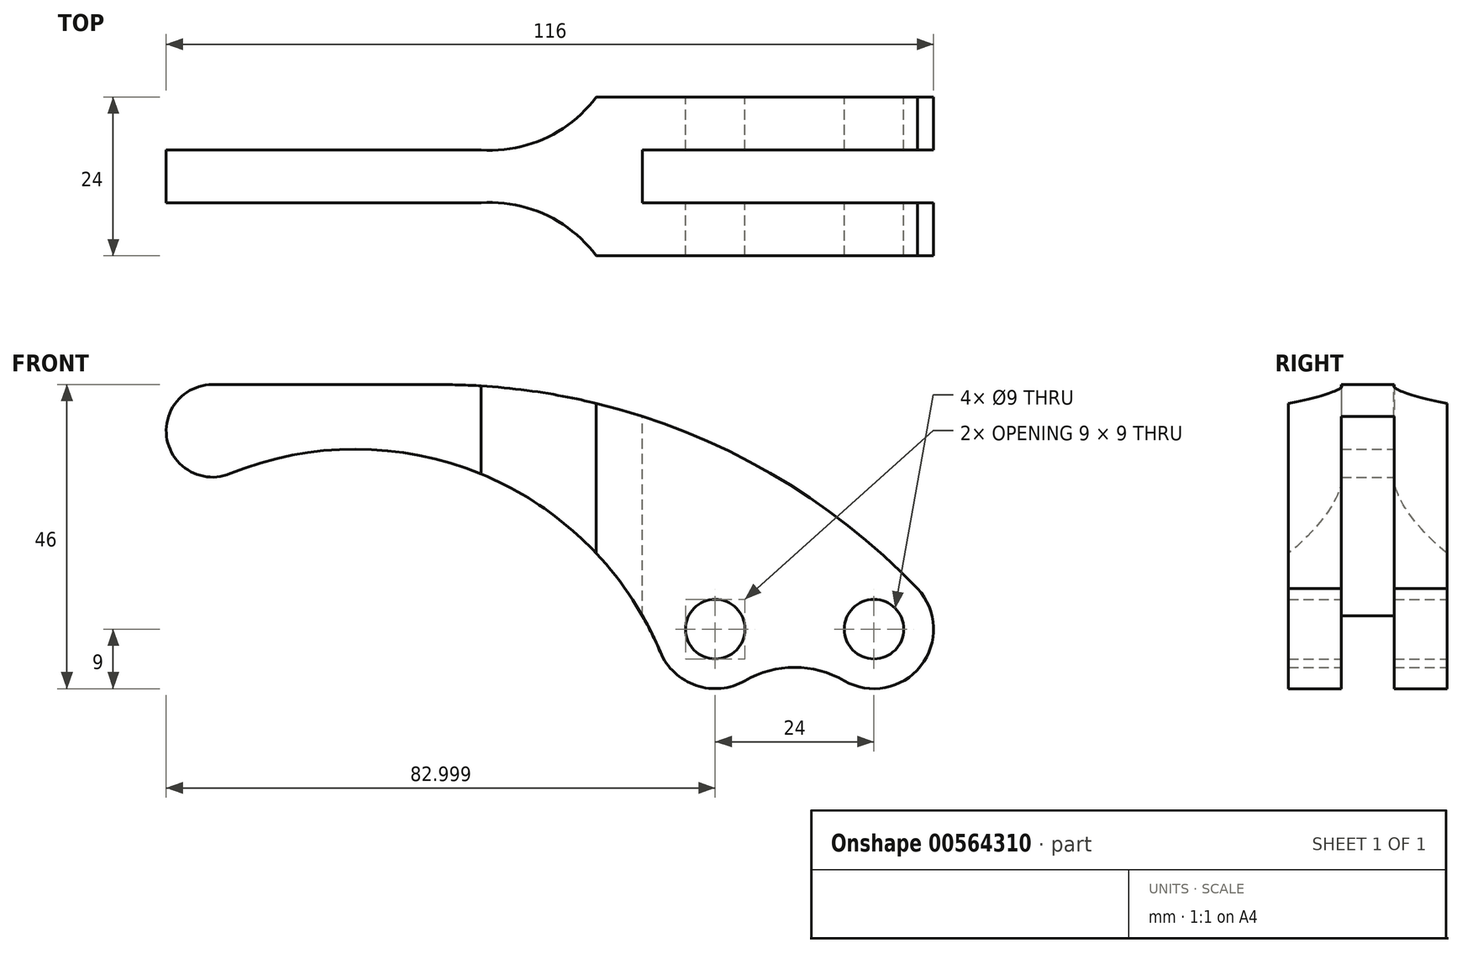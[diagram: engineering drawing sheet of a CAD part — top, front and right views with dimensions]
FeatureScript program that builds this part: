
annotation { "Feature Type Name" : "Feature", "Feature Type Description" : "" }
export const myFeature = defineFeature(function(context is Context, id is Id, definition is map)
    precondition{}
    {
        {
            var Q0;
            Q0=qCreatedBy(makeId("Front.planeOp"),FACE);
            var sketch = newSketch(context, id + "F0", { "sketchPlane" : qUnion([Q0])});
            skArc(sketch, "E0", {"start": v(-29.3, 37) * mm, "mid": v(-36.17, 28.65) * mm, "end": v(-26.65, 23.52) * mm});
            skArc(sketch, "E1", {"start": v(38.4, -3.47) * mm, "mid": v(43.82, -8.53) * mm, "end": v(51.2, -7.8) * mm});
            skArc(sketch, "E2", {"start": v(66.2, -7.8) * mm, "mid": v(77.82, -5.5) * mm, "end": v(77.1, 6.32) * mm});
            skArc(sketch, "E3", {"start": v(38.4, -3.47) * mm, "mid": v(11.43, 23.42) * mm, "end": v(-26.65, 23.52) * mm});
            skArc(sketch, "E4", {"start": v(66.2, -7.8) * mm, "mid": v(58.7, -5.78) * mm, "end": v(51.2, -7.8) * mm});
            skLineSegment(sketch, "E5", {"start": v(-29.3, 37) * mm, "end": v(5.03, 37) * mm});
            skArc(sketch, "E6", {"start": v(77.28, 6.14) * mm, "mid": v(44.31, 28.96) * mm, "end": v(5.03, 37) * mm});
            skCircle(sketch, "E7", {"center": v(46.7, 0) * mm, "radius": 4.5 * mm});
            skCircle(sketch, "E8", {"center": v(70.7, 0) * mm, "radius": 4.5 * mm});
            skSolve(sketch);
        }
        {
            var Q0;
            Q0=makeQuery(id+"F0.imprint","IMPRINT",FACE,{"disambiguationData":[TD([[makeQuery(id+"F0.imprint","IMPRINT",EDGE,{"derivedFrom":sQuery(id+"F0.wireOp",EDGE,"E0")}),1.0]])]});
            extrude(context, id + "F1", {"entities" : qUnion([Q0]), "depth" : 24 * mm, "offsetDistance" : 25 * mm});
        }
        {
            var Q0;
            Q0=qCreatedBy(makeId("Top.planeOp"),FACE);
            var sketch = newSketch(context, id + "F2", { "sketchPlane" : qUnion([Q0])});
            skLineSegment(sketch, "E9", {"start": v(-36.3, -24) * mm, "end": v(-36.3, 0) * mm});
            skArc(sketch, "E10", {"start": v(28.7, -24) * mm, "mid": v(21.01, -17.78) * mm, "end": v(11.29, -16) * mm});
            skLineSegment(sketch, "E11", {"start": v(-36.3, -24) * mm, "end": v(28.7, -24) * mm});
            skLineSegment(sketch, "E12", {"start": v(-36.3, -16) * mm, "end": v(14.04, -16) * mm});
            skLineSegment(sketch, "E13", {"start": v(-36.3, -16) * mm, "end": v(-36.3, -24) * mm});
            skLineSegment(sketch, "E14", {"start": v(-36.3, -24) * mm, "end": v(-36.3, -16) * mm});
            skLineSegment(sketch, "E15", {"start": v(-36.3, -12) * mm, "end": v(88.73, -12) * mm, "construction": true});
            skArc(sketch, "E16.MirrorCS", {"start": v(28.7, 0) * mm, "mid": v(21.01, -6.22) * mm, "end": v(11.29, -8) * mm});
            skLineSegment(sketch, "E17.MirrorCS", {"start": v(-36.3, 0) * mm, "end": v(28.7, 0) * mm});
            skLineSegment(sketch, "E18.MirrorCS", {"start": v(-36.3, 0) * mm, "end": v(-36.3, -8) * mm});
            skLineSegment(sketch, "E19.MirrorCS", {"start": v(-36.3, -8) * mm, "end": v(14.04, -8) * mm});
            skLineSegment(sketch, "E20", {"start": v(79.7, 0) * mm, "end": v(79.7, -24) * mm, "construction": true});
            skLineSegment(sketch, "E21.bottom", {"start": v(79.7, -16) * mm, "end": v(35.7, -16) * mm});
            skLineSegment(sketch, "E21.top", {"start": v(79.7, -8) * mm, "end": v(35.7, -8) * mm});
            skLineSegment(sketch, "E21.left", {"start": v(79.7, -16) * mm, "end": v(79.7, -8) * mm});
            skLineSegment(sketch, "E21.right", {"start": v(35.7, -16) * mm, "end": v(35.7, -8) * mm});
            skSolve(sketch);
        }
        {
            var Q0;
            Q0 = qSketchRegion(id + "F2", true);
            extrude(context, id + "F3", {"entities" : qUnion([Q0]), "operationType" : NewBodyOperationType.REMOVE, "oppositeDirection" : true, "depth" : 500 * mm, "offsetDistance" : 25 * mm, "hasSecondDirection" : true, "secondDirectionOppositeDirection" : false, "secondDirectionDepth" : 500 * mm});
        }
    });
